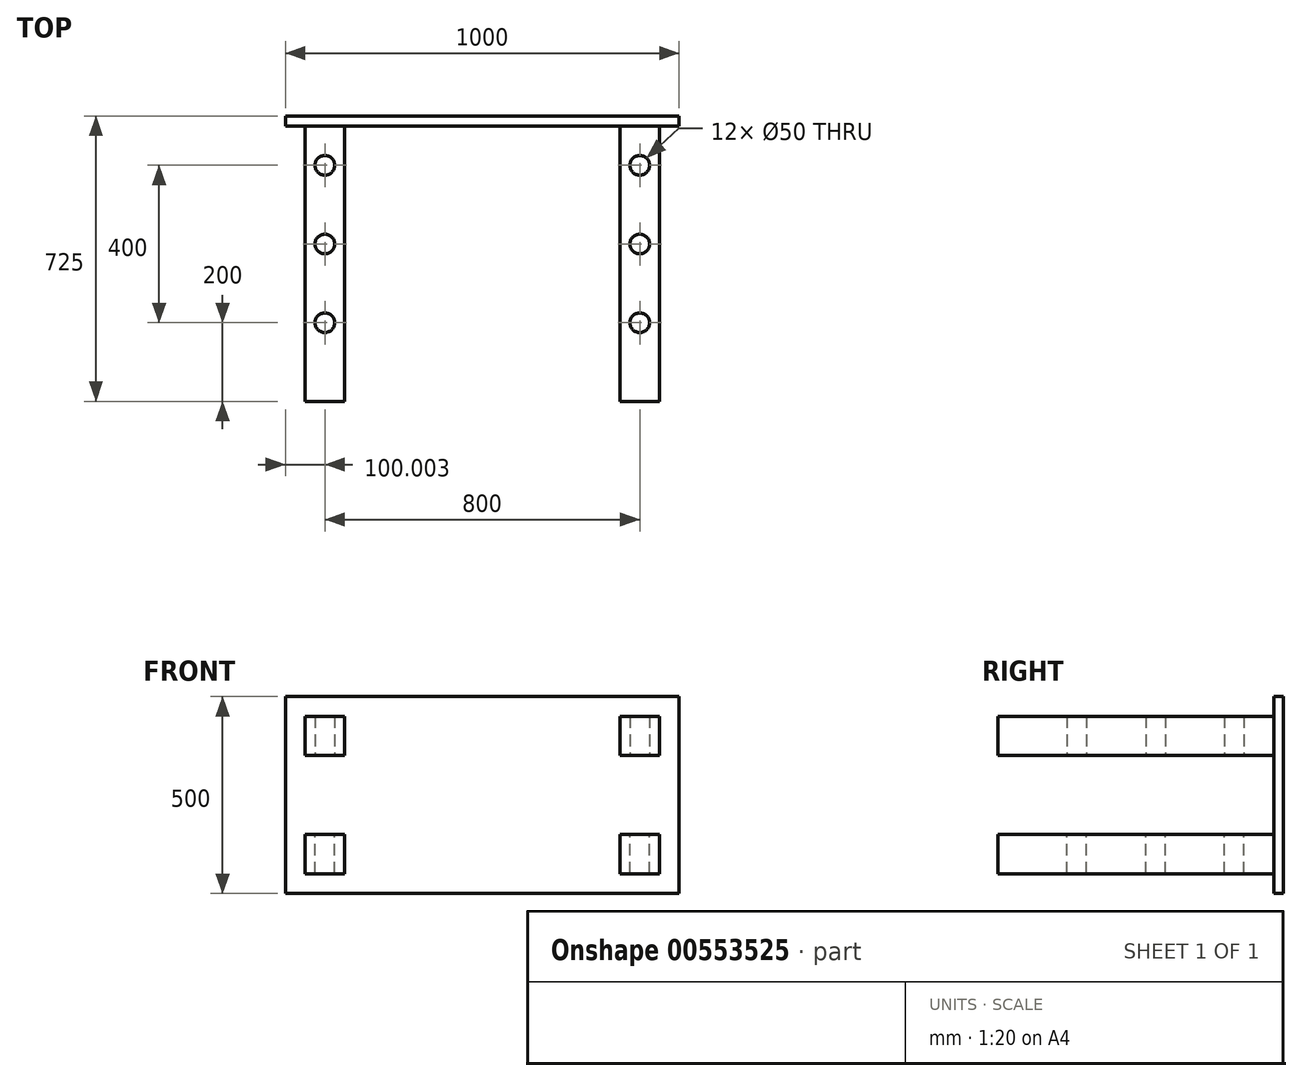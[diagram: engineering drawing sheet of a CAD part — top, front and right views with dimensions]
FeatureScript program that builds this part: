
annotation { "Feature Type Name" : "Feature", "Feature Type Description" : "" }
export const myFeature = defineFeature(function(context is Context, id is Id, definition is map)
    precondition{}
    {
        {
            var Q0;
            Q0=qCreatedBy(makeId("Front.planeOp"),FACE);
            var sketch = newSketch(context, id + "F0", { "sketchPlane" : qUnion([Q0])});
            skLineSegment(sketch, "E0.bottom", {"start": v(-106.6, 210.35) * mm, "end": v(393.4, 210.35) * mm});
            skLineSegment(sketch, "E0.top", {"start": v(-106.6, -39.65) * mm, "end": v(393.4, -39.65) * mm});
            skLineSegment(sketch, "E0.left", {"start": v(-106.6, 210.35) * mm, "end": v(-106.6, -39.65) * mm});
            skLineSegment(sketch, "E0.right", {"start": v(393.4, 210.35) * mm, "end": v(393.4, -39.65) * mm});
            skSolve(sketch);
        }
        {
            var Q0;
            Q0=makeQuery(id+"F0.imprint","IMPRINT",FACE,{"disambiguationData":[TD([[makeQuery(id+"F0.imprint","IMPRINT",EDGE,{"derivedFrom":sQuery(id+"F0.wireOp",EDGE,"E0.bottom")}),-1.0]])]});
            extrude(context, id + "F1", {"entities" : qUnion([Q0]), "depth" : 25 * mm, "offsetDistance" : 25 * mm});
        }
        {
            var Q0;
            Q0=qCreatedBy(makeId("Front.planeOp"),FACE);
            var sketch = newSketch(context, id + "F2", { "sketchPlane" : qUnion([Q0])});
            skLineSegment(sketch, "E1.bottom", {"start": v(-56.6, 110.35) * mm, "end": v(43.4, 110.35) * mm});
            skLineSegment(sketch, "E1.top", {"start": v(-56.6, 10.35) * mm, "end": v(43.4, 10.35) * mm});
            skLineSegment(sketch, "E1.left", {"start": v(-56.6, 110.35) * mm, "end": v(-56.6, 10.35) * mm});
            skLineSegment(sketch, "E1.right", {"start": v(43.4, 110.35) * mm, "end": v(43.4, 10.35) * mm});
            skSolve(sketch);
        }
        {
            var Q0;
            Q0 = qSketchRegion(id + "F2", true);
            extrude(context, id + "F3", {"entities" : qUnion([Q0]), "operationType" : NewBodyOperationType.ADD, "depth" : 725 * mm, "offsetDistance" : 25 * mm});
        }
        {
            var Q0;
            Q0=makeQuery(id+"F3.opExtrude","SWEPT_FACE",FACE,{"disambiguationData":[OSD([sQuery(id+"F2.wireOp",EDGE,"E1.bottom")])]});
            var sketch = newSketch(context, id + "F4", { "sketchPlane" : qUnion([Q0])});
            skPoint(sketch, "E2", {"position": v(-6.6, -525) * mm});
            skPoint(sketch, "E2.positionSnap0", {"position": v(-6.6, -725) * mm});
            skPoint(sketch, "E3", {"position": v(-6.6, -325) * mm});
            skPoint(sketch, "E4", {"position": v(-6.6, -125) * mm});
            skSolve(sketch);
        }
        {
            var Q0;
            Q0=sQuery(id+"F4.wireOp",VERTEX,"E4");
            var Q1;
            Q1=sQuery(id+"F4.wireOp",VERTEX,"E3");
            var Q2;
            Q2=sQuery(id+"F4.wireOp",VERTEX,"E2");
            var Q3;
            Q3=makeQuery(id+"F1.opExtrude","SWEPT_BODY",BODY,{"disambiguationData":[OSD([sQuery(id+"F0.wireOp",EDGE,"E0.bottom"),sQuery(id+"F0.wireOp",EDGE,"E0.top"),sQuery(id+"F0.wireOp",EDGE,"E0.left"),sQuery(id+"F0.wireOp",EDGE,"E0.right")])]});
            hole(context, id + "F5", {"style" : HoleStyle.SIMPLE, "endStyle" : HoleEndStyle.THROUGH, "holeDiameter" : 50 * mm, "isTappedThrough" : true, "tappedDepth" : 12 * mm, "tapClearance" : 3, "locations" : qUnion([Q0, Q1, Q2]), "scope" : qUnion([Q3])});
        }
        {
            var Q0;
            Q0=makeQuery(id+"F1.opExtrude","SWEPT_FACE",FACE,{"disambiguationData":[OSD([sQuery(id+"F0.wireOp",EDGE,"E0.right")])]});
            cPlane(context, id + "F6", {"entities" : qUnion([Q0]), "cplaneType" : CPlaneType.OFFSET, "offset" : 0 * mm, "oppositeDirection" : true, "width" : 150 * mm, "height" : 150 * mm});
        }
        {
            var Q0;
            Q0=makeQuery(id+"F1.opExtrude","SWEPT_BODY",BODY,{"disambiguationData":[OSD([sQuery(id+"F0.wireOp",EDGE,"E0.bottom"),sQuery(id+"F0.wireOp",EDGE,"E0.top"),sQuery(id+"F0.wireOp",EDGE,"E0.left"),sQuery(id+"F0.wireOp",EDGE,"E0.right")])]});
            var Q1;
            Q1=qCreatedBy(id+"F6.planeOp",FACE);
            mirror(context, id + "F7", {"operationType" : NewBodyOperationType.ADD, "entities" : qUnion([Q0]), "mirrorPlane" : qUnion([Q1])});
        }
        {
            var Q0;
            {var subQ0=makeQuery(id+"F1.opExtrude","SWEPT_FACE",FACE,{"disambiguationData":[OSD([sQuery(id+"F0.wireOp",EDGE,"E0.bottom")])]});Q0=makeQuery(id+"F7.boolean.opBoolean","MERGE",FACE,{"derivedFrom":[subQ0,makeQuery(id+"F7.opPattern","COPY",FACE,{"derivedFrom":subQ0,"instanceName":"1"})]});}
            cPlane(context, id + "F8", {"entities" : qUnion([Q0]), "cplaneType" : CPlaneType.OFFSET, "offset" : 0 * mm, "width" : 150 * mm, "height" : 150 * mm});
        }
        {
            var Q0;
            Q0=makeQuery(id+"F1.opExtrude","SWEPT_BODY",BODY,{"disambiguationData":[OSD([sQuery(id+"F0.wireOp",EDGE,"E0.bottom"),sQuery(id+"F0.wireOp",EDGE,"E0.top"),sQuery(id+"F0.wireOp",EDGE,"E0.left"),sQuery(id+"F0.wireOp",EDGE,"E0.right")])]});
            var Q1;
            Q1=qCreatedBy(id+"F8.planeOp",FACE);
            mirror(context, id + "F9", {"operationType" : NewBodyOperationType.ADD, "entities" : qUnion([Q0]), "mirrorPlane" : qUnion([Q1])});
        }
    });
